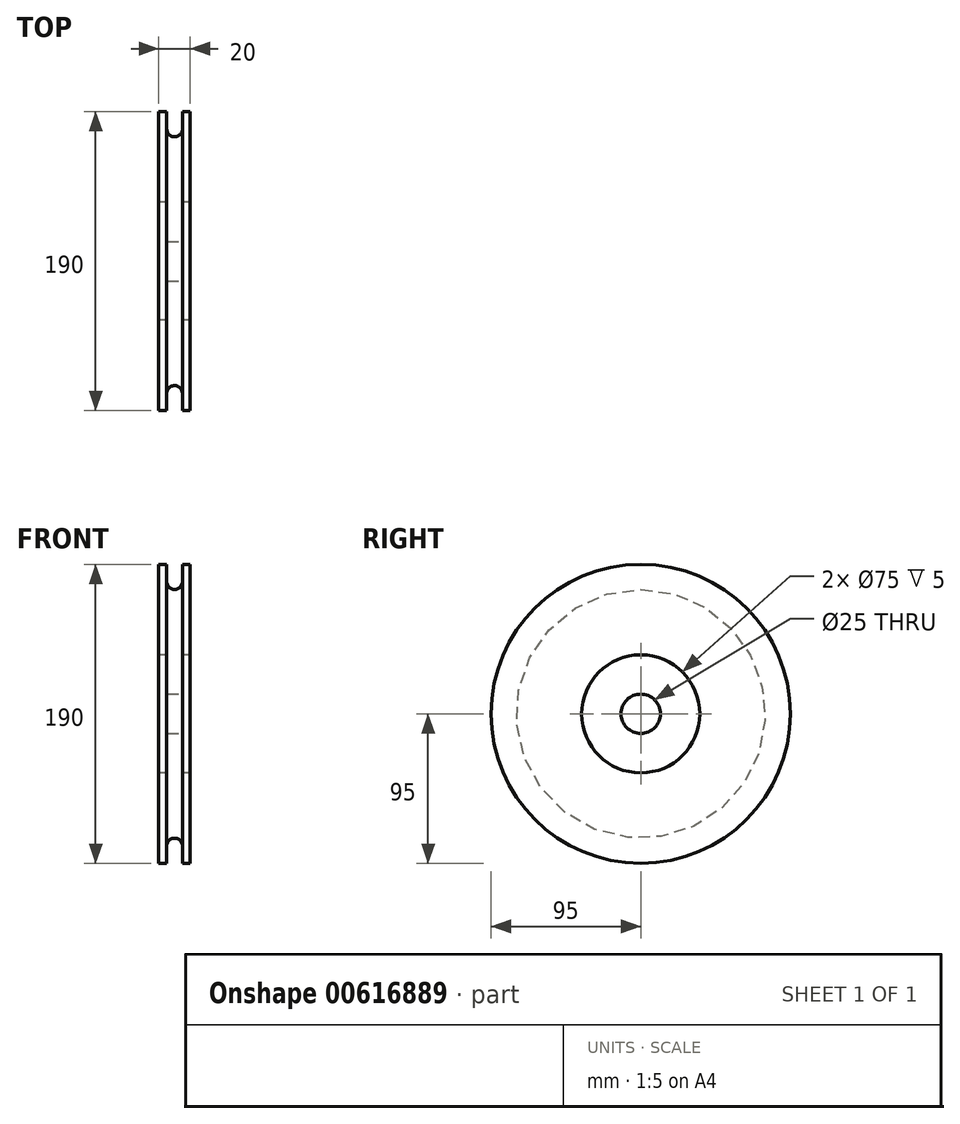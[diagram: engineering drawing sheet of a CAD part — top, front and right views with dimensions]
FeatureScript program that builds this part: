
annotation { "Feature Type Name" : "Feature", "Feature Type Description" : "" }
export const myFeature = defineFeature(function(context is Context, id is Id, definition is map)
    precondition{}
    {
        {
            var Q0;
            Q0=qCreatedBy(makeId("Front.planeOp"),FACE);
            var sketch = newSketch(context, id + "F0", { "sketchPlane" : qUnion([Q0])});
            skLineSegment(sketch, "E0", {"start": v(0, 37.5) * mm, "end": v(0, 95) * mm});
            skLineSegment(sketch, "E1", {"start": v(0, 95) * mm, "end": v(5, 95) * mm});
            skLineSegment(sketch, "E2", {"start": v(5, 95) * mm, "end": v(5, 84) * mm});
            skLineSegment(sketch, "E3", {"start": v(15, 84) * mm, "end": v(15, 95) * mm});
            skLineSegment(sketch, "E4", {"start": v(15, 95) * mm, "end": v(20, 95) * mm});
            skLineSegment(sketch, "E5", {"start": v(20, 95) * mm, "end": v(20, 37.5) * mm});
            skLineSegment(sketch, "E6", {"start": v(20, 37.5) * mm, "end": v(0, 37.5) * mm});
            skArc(sketch, "E7", {"start": v(5, 84) * mm, "mid": v(10, 79) * mm, "end": v(15, 84) * mm});
            skLineSegment(sketch, "E8", {"start": v(0, 0) * mm, "end": v(56.3, 0) * mm, "construction": true});
            skSolve(sketch);
        }
        {
            var Q0;
            Q0=qSketchRegion(id+"F0",true);
            var Q1;
            Q1=sQuery(id+"F0.wireOp",EDGE,"E8");
            revolve(context, id + "F1", {"surfaceOperationType" : NewSurfaceOperationType.NEW, "entities" : qUnion([Q0]), "axis" : qUnion([Q1]), "revolveType" : RevolveType.FULL});
        }
        {
            var Q0;
            Q0=makeQuery(id+"F1.opRevolve","SWEPT_FACE",FACE,{"disambiguationData":[OSD([sQuery(id+"F0.wireOp",EDGE,"E5")])]});
            var sketch = newSketch(context, id + "F2", { "sketchPlane" : qUnion([Q0])});
            skCircle(sketch, "E9", {"center": v(0, 0) * mm, "radius": 12.5 * mm});
            skCircle(sketch, "E10.0", {"center": v(0, 0) * mm, "radius": 37.5 * mm});
            skSolve(sketch);
        }
        {
            var Q0;
            Q0=qSketchRegion(id+"F2",true);
            extrude(context, id + "F3", {"entities" : qUnion([Q0]), "operationType" : NewBodyOperationType.ADD, "oppositeDirection" : true, "depth" : 15 * mm, "offsetDistance" : 25 * mm, "hasSecondDirection" : true, "secondDirectionOppositeDirection" : true, "secondDirectionDepth" : 5 * mm});
        }
    });
